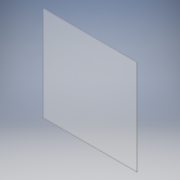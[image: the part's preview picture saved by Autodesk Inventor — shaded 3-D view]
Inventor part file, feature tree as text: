
AUTODESK INVENTOR PART (.ipt)
format: ipt  version: 2019.4 (Build 234330000, 330)  size: 104,960 bytes
history: native  units: mm
features: other x1, extrude x1, sketch x1
ambient origin geometry x8: Origin, YZ Plane, XZ Plane, XY Plane, X Axis, Y Axis, Z Axis, Center Point
bodies: Body1 (feature_tree)
feature tree (3):
  other  "Sólido1"
  extrude  "Extrusão1"  Depth=1200.0mm
  sketch  "Esboço1"  dims[d0=1212.36mm d1=1200.0mm d2=10.0mm d3=0.0mm]
